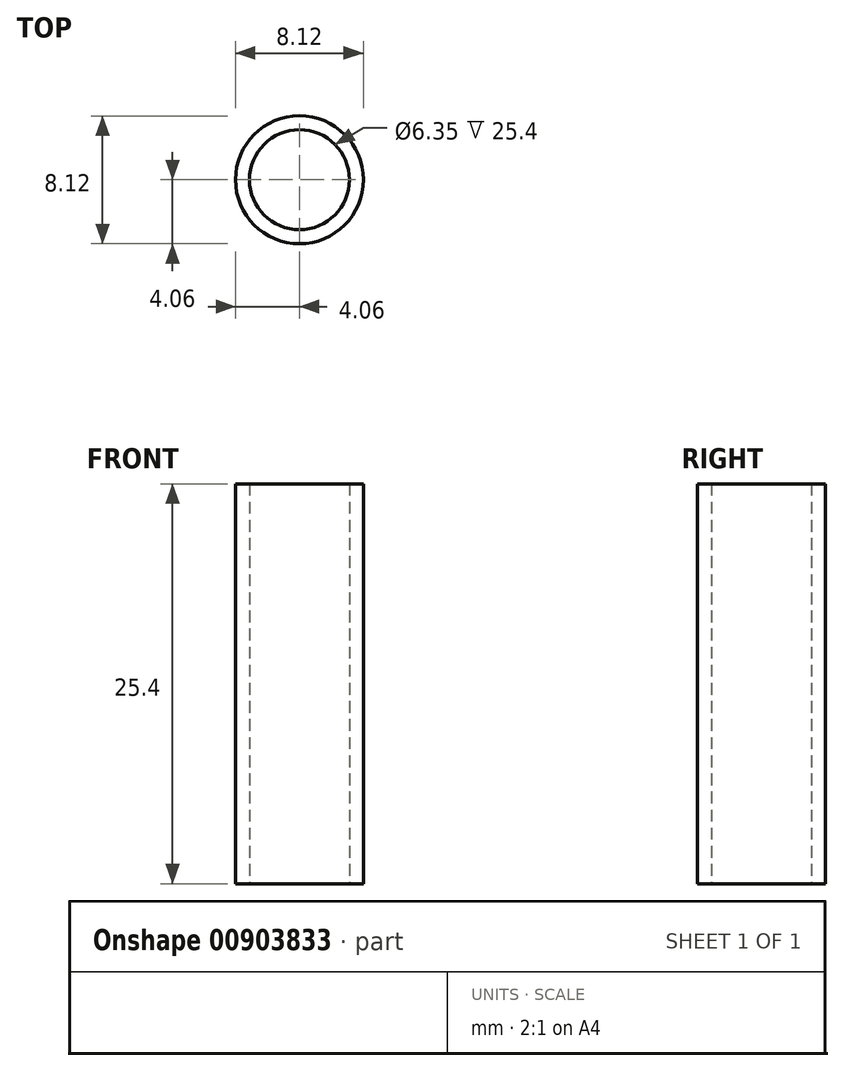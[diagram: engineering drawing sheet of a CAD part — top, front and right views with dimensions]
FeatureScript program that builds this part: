
annotation { "Feature Type Name" : "Feature", "Feature Type Description" : "" }
export const myFeature = defineFeature(function(context is Context, id is Id, definition is map)
    precondition{}
    {
        {
            var Q0;
            Q0=qCreatedBy(makeId("Top.planeOp"),FACE);
            var sketch = newSketch(context, id + "F0", { "sketchPlane" : qUnion([Q0])});
            skCircle(sketch, "E0", {"center": v(0, 0) * mm, "radius": 3.18 * mm});
            skCircle(sketch, "E1", {"center": v(0, 0) * mm, "radius": 4.06 * mm});
            skSolve(sketch);
        }
        {
            var Q0;
            Q0 = qSketchRegion(id + "F0", true);
            extrude(context, id + "F1", {"entities" : qUnion([Q0]), "depth" : 25.4 * mm, "offsetDistance" : 25.4 * mm});
        }
    });
